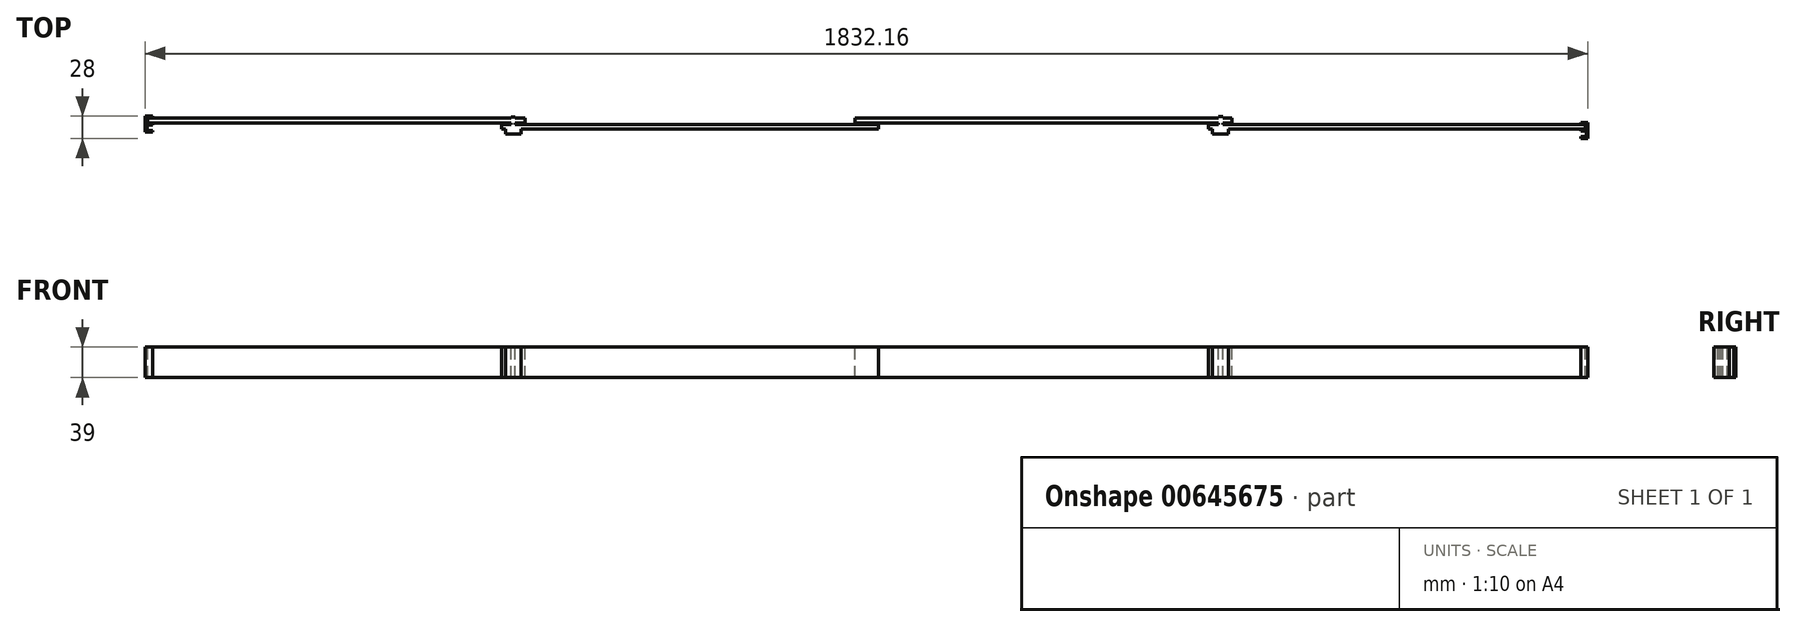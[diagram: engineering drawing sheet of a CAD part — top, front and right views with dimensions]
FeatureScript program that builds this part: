
annotation { "Feature Type Name" : "Feature", "Feature Type Description" : "" }
export const myFeature = defineFeature(function(context is Context, id is Id, definition is map)
    precondition{}
    {
        {
            var Q0;
            Q0=qCreatedBy(makeId("Top.planeOp"),FACE);
            var sketch = newSketch(context, id + "F0", { "sketchPlane" : qUnion([Q0])});
            skLineSegment(sketch, "E0.bottom", {"start": v(-1511.4, -759.82) * mm, "end": v(-1032.4, -759.82) * mm});
            skLineSegment(sketch, "E0.top", {"start": v(-1511.4, -765.82) * mm, "end": v(-1032.4, -765.82) * mm});
            skLineSegment(sketch, "E0.left", {"start": v(-1511.4, -759.82) * mm, "end": v(-1511.4, -765.82) * mm});
            skLineSegment(sketch, "E0.right", {"start": v(-1032.4, -759.82) * mm, "end": v(-1032.4, -765.82) * mm});
            skLineSegment(sketch, "E1.bottom", {"start": v(-1062.4, -767.82) * mm, "end": v(-583.4, -767.82) * mm});
            skLineSegment(sketch, "E1.top", {"start": v(-1062.4, -773.82) * mm, "end": v(-583.4, -773.82) * mm});
            skLineSegment(sketch, "E1.left", {"start": v(-1062.4, -767.82) * mm, "end": v(-1062.4, -773.82) * mm});
            skLineSegment(sketch, "E1.right", {"start": v(-583.4, -767.82) * mm, "end": v(-583.4, -773.82) * mm});
            skLineSegment(sketch, "E2.bottom", {"start": v(-613.4, -759.82) * mm, "end": v(-134.4, -759.82) * mm});
            skLineSegment(sketch, "E2.top", {"start": v(-613.4, -765.82) * mm, "end": v(-134.4, -765.82) * mm});
            skLineSegment(sketch, "E2.left", {"start": v(-613.4, -759.82) * mm, "end": v(-613.4, -765.82) * mm});
            skLineSegment(sketch, "E2.right", {"start": v(-134.4, -759.82) * mm, "end": v(-134.4, -765.82) * mm});
            skLineSegment(sketch, "E3.bottom", {"start": v(-164.4, -767.82) * mm, "end": v(314.6, -767.82) * mm});
            skLineSegment(sketch, "E3.top", {"start": v(-164.4, -773.82) * mm, "end": v(314.6, -773.82) * mm});
            skLineSegment(sketch, "E3.left", {"start": v(-164.4, -767.82) * mm, "end": v(-164.4, -773.82) * mm});
            skLineSegment(sketch, "E3.right", {"start": v(314.6, -767.82) * mm, "end": v(314.6, -773.82) * mm});
            skLineSegment(sketch, "E4", {"start": v(-1505.55, -759.32) * mm, "end": v(-1512.55, -759.32) * mm});
            skLineSegment(sketch, "E5", {"start": v(-1512.55, -759.32) * mm, "end": v(-1512.55, -766.32) * mm});
            skLineSegment(sketch, "E6", {"start": v(-1512.55, -766.32) * mm, "end": v(-1505.55, -766.32) * mm});
            skLineSegment(sketch, "E7", {"start": v(-1505.55, -766.32) * mm, "end": v(-1505.55, -768.32) * mm});
            skLineSegment(sketch, "E8", {"start": v(-1505.55, -768.32) * mm, "end": v(-1512.55, -768.32) * mm});
            skLineSegment(sketch, "E9", {"start": v(-1512.55, -768.32) * mm, "end": v(-1512.55, -775.32) * mm});
            skLineSegment(sketch, "E10", {"start": v(-1512.55, -775.32) * mm, "end": v(-1505.55, -775.32) * mm});
            skLineSegment(sketch, "E11", {"start": v(-1505.55, -775.32) * mm, "end": v(-1505.55, -777.32) * mm});
            skLineSegment(sketch, "E12", {"start": v(-1505.55, -777.32) * mm, "end": v(-1514.55, -777.32) * mm});
            skLineSegment(sketch, "E13", {"start": v(-1514.55, -777.32) * mm, "end": v(-1514.55, -757.32) * mm});
            skLineSegment(sketch, "E14", {"start": v(-1514.55, -757.32) * mm, "end": v(-1505.55, -757.32) * mm});
            skLineSegment(sketch, "E15", {"start": v(-1505.55, -757.32) * mm, "end": v(-1505.55, -759.32) * mm});
            skLineSegment(sketch, "E16", {"start": v(308.6, -783.32) * mm, "end": v(315.6, -783.32) * mm});
            skLineSegment(sketch, "E17", {"start": v(315.6, -783.32) * mm, "end": v(315.6, -776.32) * mm});
            skLineSegment(sketch, "E18", {"start": v(315.6, -776.32) * mm, "end": v(308.6, -776.32) * mm});
            skLineSegment(sketch, "E19", {"start": v(308.6, -776.32) * mm, "end": v(308.6, -774.32) * mm});
            skLineSegment(sketch, "E20", {"start": v(308.6, -774.32) * mm, "end": v(315.6, -774.32) * mm});
            skLineSegment(sketch, "E21", {"start": v(315.6, -774.32) * mm, "end": v(315.6, -767.32) * mm});
            skLineSegment(sketch, "E22", {"start": v(315.6, -767.32) * mm, "end": v(308.6, -767.32) * mm});
            skLineSegment(sketch, "E23", {"start": v(308.6, -767.32) * mm, "end": v(308.6, -765.32) * mm});
            skLineSegment(sketch, "E24", {"start": v(308.6, -765.32) * mm, "end": v(317.6, -765.32) * mm});
            skLineSegment(sketch, "E25", {"start": v(317.6, -765.32) * mm, "end": v(317.6, -785.32) * mm});
            skLineSegment(sketch, "E26", {"start": v(317.6, -785.32) * mm, "end": v(308.6, -785.32) * mm});
            skLineSegment(sketch, "E27", {"start": v(308.6, -785.32) * mm, "end": v(308.6, -783.32) * mm});
            skLineSegment(sketch, "E28.bottom", {"start": v(-1057.21, -767.82) * mm, "end": v(-1037.21, -767.82) * mm});
            skLineSegment(sketch, "E28.top", {"start": v(-1057.21, -779.82) * mm, "end": v(-1037.21, -779.82) * mm});
            skLineSegment(sketch, "E28.left", {"start": v(-1057.21, -767.82) * mm, "end": v(-1057.21, -779.82) * mm});
            skLineSegment(sketch, "E28.right", {"start": v(-1037.21, -767.82) * mm, "end": v(-1037.21, -779.82) * mm});
            skLineSegment(sketch, "E29.bottom", {"start": v(-1050.1, -758.1) * mm, "end": v(-1045.17, -758.1) * mm});
            skLineSegment(sketch, "E29.top", {"start": v(-1050.1, -770.97) * mm, "end": v(-1045.17, -770.97) * mm});
            skLineSegment(sketch, "E29.left", {"start": v(-1050.1, -758.1) * mm, "end": v(-1050.1, -770.97) * mm});
            skLineSegment(sketch, "E29.right", {"start": v(-1045.17, -758.1) * mm, "end": v(-1045.17, -770.97) * mm});
            skLineSegment(sketch, "E30.bottom", {"start": v(-158.9, -767.82) * mm, "end": v(-138.9, -767.82) * mm});
            skLineSegment(sketch, "E30.top", {"start": v(-158.9, -779.82) * mm, "end": v(-138.9, -779.82) * mm});
            skLineSegment(sketch, "E30.left", {"start": v(-158.9, -767.82) * mm, "end": v(-158.9, -779.82) * mm});
            skLineSegment(sketch, "E30.right", {"start": v(-138.9, -767.82) * mm, "end": v(-138.9, -779.82) * mm});
            skLineSegment(sketch, "E31.bottom", {"start": v(-151.74, -757.75) * mm, "end": v(-145.74, -757.75) * mm});
            skLineSegment(sketch, "E31.top", {"start": v(-151.74, -770.75) * mm, "end": v(-145.74, -770.75) * mm});
            skLineSegment(sketch, "E31.left", {"start": v(-151.74, -757.75) * mm, "end": v(-151.74, -770.75) * mm});
            skLineSegment(sketch, "E31.right", {"start": v(-145.74, -757.75) * mm, "end": v(-145.74, -770.75) * mm});
            skSolve(sketch);
        }
        {
            var Q0;
            {var subQ5=sQuery(id+"F0.wireOp",EDGE,"E28.top");Q0=makeQuery(id+"F0.imprint","IMPRINT",FACE,{"disambiguationData":[TD([[makeQuery(id+"F0.imprint","IMPRINT",EDGE,{"derivedFrom":subQ5}),1.0]])]});}
            var Q1;
            {var subQ12=sQuery(id+"F0.wireOp",EDGE,"E29.top");Q1=makeQuery(id+"F0.imprint","IMPRINT",FACE,{"disambiguationData":[TD([[makeQuery(id+"F0.imprint","IMPRINT",EDGE,{"derivedFrom":subQ12}),-1.0]])]});}
            var Q2;
            {var subQ0=sQuery(id+"F0.wireOp",EDGE,"E1.left");Q2=makeQuery(id+"F0.imprint","IMPRINT",FACE,{"disambiguationData":[TD([[makeQuery(id+"F0.imprint","IMPRINT",EDGE,{"derivedFrom":subQ0}),1.0]])]});}
            var Q3;
            {var subQ0=sQuery(id+"F0.wireOp",EDGE,"E0.left");Q3=makeQuery(id+"F0.imprint","IMPRINT",FACE,{"disambiguationData":[TD([[makeQuery(id+"F0.imprint","IMPRINT",EDGE,{"derivedFrom":subQ0}),1.0]])]});}
            var Q4;
            {var subQ0=sQuery(id+"F0.wireOp",EDGE,"E29.left");var subQ1=sQuery(id+"F0.wireOp",EDGE,"E0.bottom");var subQ2=makeQuery(id+"F0.imprint","INTERSECT",VERTEX,{"derivedFrom":[subQ1,subQ0]});Q4=makeQuery(id+"F0.imprint","IMPRINT",FACE,{"disambiguationData":[TD([[makeQuery(id+"F0.imprint","IMPRINT",EDGE,{"disambiguationData":[TD([[subQ2,-1.0]])],"derivedFrom":subQ1}),-1.0]])]});}
            var Q5;
            {var subQ5=sQuery(id+"F0.wireOp",EDGE,"E29.top");Q5=makeQuery(id+"F0.imprint","IMPRINT",FACE,{"disambiguationData":[TD([[makeQuery(id+"F0.imprint","IMPRINT",EDGE,{"derivedFrom":subQ5}),1.0]])]});}
            var Q6;
            {var subQ0=sQuery(id+"F0.wireOp",EDGE,"E29.left");var subQ1=sQuery(id+"F0.wireOp",EDGE,"E0.top");var subQ2=makeQuery(id+"F0.imprint","INTERSECT",VERTEX,{"derivedFrom":[subQ1,subQ0]});Q6=makeQuery(id+"F0.imprint","IMPRINT",FACE,{"disambiguationData":[TD([[makeQuery(id+"F0.imprint","IMPRINT",EDGE,{"disambiguationData":[TD([[subQ2,-1.0]])],"derivedFrom":subQ1}),-1.0]])]});}
            var Q7;
            {var subQ5=sQuery(id+"F0.wireOp",EDGE,"E29.bottom");Q7=makeQuery(id+"F0.imprint","IMPRINT",FACE,{"disambiguationData":[TD([[makeQuery(id+"F0.imprint","IMPRINT",EDGE,{"derivedFrom":subQ5}),-1.0]])]});}
            var Q8;
            {var subQ0=sQuery(id+"F0.wireOp",EDGE,"E0.right");Q8=makeQuery(id+"F0.imprint","IMPRINT",FACE,{"disambiguationData":[TD([[makeQuery(id+"F0.imprint","IMPRINT",EDGE,{"derivedFrom":subQ0}),-1.0]])]});}
            var Q9;
            Q9=makeQuery(id+"F0.imprint","IMPRINT",FACE,{"disambiguationData":[TD([[makeQuery(id+"F0.imprint","IMPRINT",EDGE,{"derivedFrom":sQuery(id+"F0.wireOp",EDGE,"E4")}),-1.0]])]});
            var Q10;
            {var subQ0=sQuery(id+"F0.wireOp",EDGE,"E1.right");Q10=makeQuery(id+"F0.imprint","IMPRINT",FACE,{"disambiguationData":[TD([[makeQuery(id+"F0.imprint","IMPRINT",EDGE,{"derivedFrom":subQ0}),-1.0]])]});}
            var Q11;
            {var subQ0=sQuery(id+"F0.wireOp",EDGE,"E2.left");Q11=makeQuery(id+"F0.imprint","IMPRINT",FACE,{"disambiguationData":[TD([[makeQuery(id+"F0.imprint","IMPRINT",EDGE,{"derivedFrom":subQ0}),1.0]])]});}
            var Q12;
            {var subQ5=sQuery(id+"F0.wireOp",EDGE,"E30.top");Q12=makeQuery(id+"F0.imprint","IMPRINT",FACE,{"disambiguationData":[TD([[makeQuery(id+"F0.imprint","IMPRINT",EDGE,{"derivedFrom":subQ5}),1.0]])]});}
            var Q13;
            {var subQ7=sQuery(id+"F0.wireOp",EDGE,"E31.top");Q13=makeQuery(id+"F0.imprint","IMPRINT",FACE,{"disambiguationData":[TD([[makeQuery(id+"F0.imprint","IMPRINT",EDGE,{"derivedFrom":subQ7}),-1.0]])]});}
            var Q14;
            {var subQ5=sQuery(id+"F0.wireOp",EDGE,"E31.top");Q14=makeQuery(id+"F0.imprint","IMPRINT",FACE,{"disambiguationData":[TD([[makeQuery(id+"F0.imprint","IMPRINT",EDGE,{"derivedFrom":subQ5}),1.0]])]});}
            var Q15;
            {var subQ0=sQuery(id+"F0.wireOp",EDGE,"E31.left");var subQ1=sQuery(id+"F0.wireOp",EDGE,"E2.top");var subQ2=makeQuery(id+"F0.imprint","INTERSECT",VERTEX,{"derivedFrom":[subQ1,subQ0]});Q15=makeQuery(id+"F0.imprint","IMPRINT",FACE,{"disambiguationData":[TD([[makeQuery(id+"F0.imprint","IMPRINT",EDGE,{"disambiguationData":[TD([[subQ2,-1.0]])],"derivedFrom":subQ1}),-1.0]])]});}
            var Q16;
            {var subQ0=sQuery(id+"F0.wireOp",EDGE,"E31.left");var subQ1=sQuery(id+"F0.wireOp",EDGE,"E2.bottom");var subQ2=makeQuery(id+"F0.imprint","INTERSECT",VERTEX,{"derivedFrom":[subQ1,subQ0]});Q16=makeQuery(id+"F0.imprint","IMPRINT",FACE,{"disambiguationData":[TD([[makeQuery(id+"F0.imprint","IMPRINT",EDGE,{"disambiguationData":[TD([[subQ2,-1.0]])],"derivedFrom":subQ1}),-1.0]])]});}
            var Q17;
            {var subQ5=sQuery(id+"F0.wireOp",EDGE,"E31.bottom");Q17=makeQuery(id+"F0.imprint","IMPRINT",FACE,{"disambiguationData":[TD([[makeQuery(id+"F0.imprint","IMPRINT",EDGE,{"derivedFrom":subQ5}),-1.0]])]});}
            var Q18;
            {var subQ0=sQuery(id+"F0.wireOp",EDGE,"E2.right");Q18=makeQuery(id+"F0.imprint","IMPRINT",FACE,{"disambiguationData":[TD([[makeQuery(id+"F0.imprint","IMPRINT",EDGE,{"derivedFrom":subQ0}),-1.0]])]});}
            var Q19;
            {var subQ0=sQuery(id+"F0.wireOp",EDGE,"E3.left");Q19=makeQuery(id+"F0.imprint","IMPRINT",FACE,{"disambiguationData":[TD([[makeQuery(id+"F0.imprint","IMPRINT",EDGE,{"derivedFrom":subQ0}),1.0]])]});}
            var Q20;
            {var subQ0=sQuery(id+"F0.wireOp",EDGE,"E3.right");Q20=makeQuery(id+"F0.imprint","IMPRINT",FACE,{"disambiguationData":[TD([[makeQuery(id+"F0.imprint","IMPRINT",EDGE,{"derivedFrom":subQ0}),-1.0]])]});}
            var Q21;
            Q21=makeQuery(id+"F0.imprint","IMPRINT",FACE,{"disambiguationData":[TD([[makeQuery(id+"F0.imprint","IMPRINT",EDGE,{"derivedFrom":sQuery(id+"F0.wireOp",EDGE,"E16")}),-1.0]])]});
            extrude(context, id + "F1", {"entities" : qUnion([Q0, Q1, Q2, Q3, Q4, Q5, Q6, Q7, Q8, Q9, Q10, Q11, Q12, Q13, Q14, Q15, Q16, Q17, Q18, Q19, Q20, Q21]), "oppositeDirection" : true, "depth" : 39 * mm, "offsetDistance" : 25 * mm});
        }
    });
